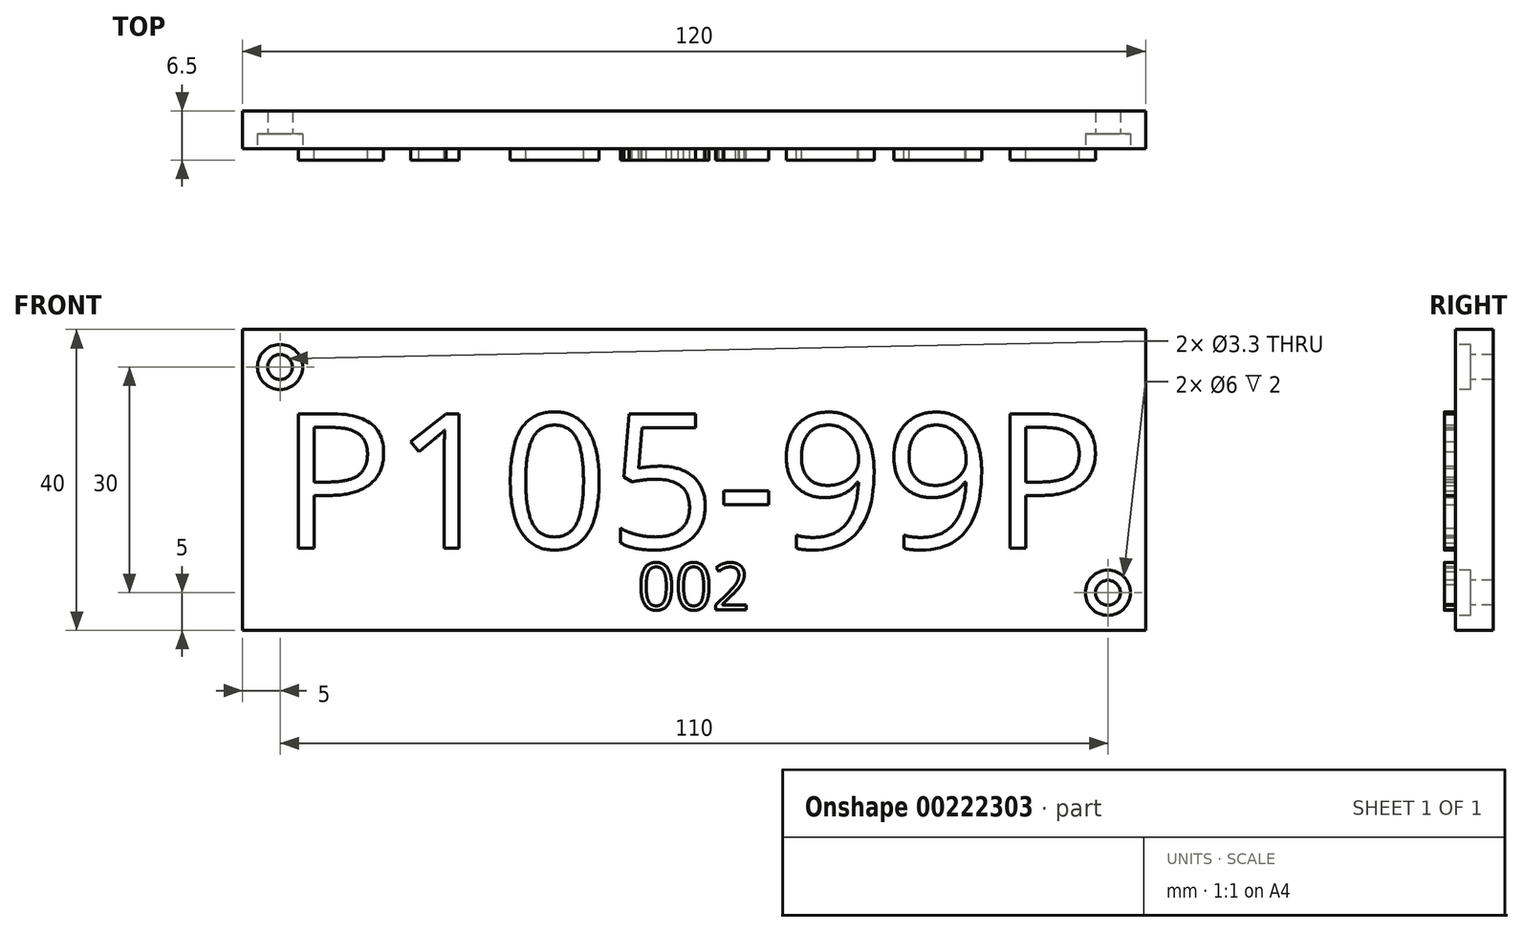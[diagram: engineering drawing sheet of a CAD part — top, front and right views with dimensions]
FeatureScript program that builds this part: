
annotation { "Feature Type Name" : "Feature", "Feature Type Description" : "" }
export const myFeature = defineFeature(function(context is Context, id is Id, definition is map)
    precondition{}
    {
        {
            var Q0;
            Q0=qCreatedBy(makeId("Front.planeOp"),FACE);
            var sketch = newSketch(context, id + "F0", { "sketchPlane" : qUnion([Q0])});
            skLineSegment(sketch, "E0.bottom", {"start": v(60, -20) * mm, "end": v(-60, -20) * mm});
            skLineSegment(sketch, "E0.top", {"start": v(60, 20) * mm, "end": v(-60, 20) * mm});
            skLineSegment(sketch, "E0.left", {"start": v(60, -20) * mm, "end": v(60, 20) * mm});
            skLineSegment(sketch, "E0.right", {"start": v(-60, -20) * mm, "end": v(-60, 20) * mm});
            skPoint(sketch, "E0.middle", {"position": v(0, 0) * mm});
            skPoint(sketch, "E1", {"position": v(-55, 15) * mm});
            skPoint(sketch, "E2", {"position": v(55, -15) * mm});
            skSolve(sketch);
        }
        {
            var Q0;
            Q0=makeQuery(id+"F0.imprint","IMPRINT",FACE,{"disambiguationData":[TD([[makeQuery(id+"F0.imprint","IMPRINT",EDGE,{"derivedFrom":sQuery(id+"F0.wireOp",EDGE,"E0.bottom")}),-1.0]])]});
            extrude(context, id + "F1", {"entities" : qUnion([Q0]), "depth" : 5 * mm});
        }
        {
            var Q0;
            Q0=makeQuery(id+"F1.opExtrude","CAP_FACE",FACE,{"disambiguationData":[OSD([sQuery(id+"F0.wireOp",EDGE,"E0.bottom"),sQuery(id+"F0.wireOp",EDGE,"E0.top"),sQuery(id+"F0.wireOp",EDGE,"E0.left"),sQuery(id+"F0.wireOp",EDGE,"E0.right")])],"isStart":false});
            var sketch = newSketch(context, id + "F2", { "sketchPlane" : qUnion([Q0])});
            skPoint(sketch, "E3", {"position": v(-55, 15) * mm});
            skPoint(sketch, "E4", {"position": v(55, -15) * mm});
            skSolve(sketch);
        }
        {
            var Q0;
            Q0=sQuery(id+"F2.wireOp",VERTEX,"E3");
            var Q1;
            Q1=sQuery(id+"F2.wireOp",VERTEX,"E4");
            var Q2;
            Q2=makeQuery(id+"F1.opExtrude","SWEPT_BODY",BODY,{"disambiguationData":[OSD([sQuery(id+"F0.wireOp",EDGE,"E0.bottom"),sQuery(id+"F0.wireOp",EDGE,"E0.top"),sQuery(id+"F0.wireOp",EDGE,"E0.left"),sQuery(id+"F0.wireOp",EDGE,"E0.right")])]});
            hole(context, id + "F3", {"style" : HoleStyle.C_BORE, "endStyle" : HoleEndStyle.THROUGH, "holeDiameter" : 3.3 * mm, "cBoreDiameter" : 6 * mm, "cBoreDepth" : 2 * mm, "locations" : qUnion([Q0, Q1]), "scope" : qUnion([Q2]), "isTappedThrough" : true});
        }
        {
            var Q0;
            Q0=makeQuery(id+"F1.opExtrude","CAP_FACE",FACE,{"disambiguationData":[OSD([sQuery(id+"F0.wireOp",EDGE,"E0.bottom"),sQuery(id+"F0.wireOp",EDGE,"E0.top"),sQuery(id+"F0.wireOp",EDGE,"E0.left"),sQuery(id+"F0.wireOp",EDGE,"E0.right")])],"isStart":false});
            var sketch = newSketch(context, id + "F4", { "sketchPlane" : qUnion([Q0])});
            skText(sketch, "E5", { "text": "P105-99P", "fontName": "OpenSans-Regular.ttf"});
            const initialGuessF4  = {"E5": [-0.055, -0.00908, 1, 0, 0.018]};
            skSetInitialGuess(sketch, initialGuessF4);
            skSolve(sketch);
        }
        {
            var Q0;
            Q0 = qSketchRegion(id + "F4", true);
            extrude(context, id + "F5", {"entities" : qUnion([Q0]), "operationType" : NewBodyOperationType.ADD, "depth" : 1.5 * mm});
        }
        {
            var Q0;
            {var subQ0=sQuery(id+"F0.wireOp",EDGE,"E0.bottom");var subQ1=sQuery(id+"F0.wireOp",EDGE,"E0.top");var subQ2=sQuery(id+"F0.wireOp",EDGE,"E0.left");var subQ3=sQuery(id+"F0.wireOp",EDGE,"E0.right");Q0=makeQuery(id+"F5.boolean.opBoolean","SPLIT",FACE,{"disambiguationData":[TD([makeQuery(id+"F1.opExtrude","SWEPT_FACE",FACE,{"disambiguationData":[OSD([subQ0])]})])],"derivedFrom":makeQuery(id+"F1.opExtrude","CAP_FACE",FACE,{"disambiguationData":[OSD([subQ0,subQ1,subQ2,subQ3])],"isStart":false})});}
            var sketch = newSketch(context, id + "F6", { "sketchPlane" : qUnion([Q0])});
            skText(sketch, "E6", { "text": "002", "fontName": "OpenSans-Regular.ttf"});
            const initialGuessF6  = {"E6": [-0.0075, -0.01726, 1, 0, 0.00626]};
            skSetInitialGuess(sketch, initialGuessF6);
            skSolve(sketch);
        }
        {
            var Q0;
            Q0 = qSketchRegion(id + "F6", true);
            extrude(context, id + "F7", {"entities" : qUnion([Q0]), "operationType" : NewBodyOperationType.ADD, "depth" : 1.5 * mm});
        }
    });
